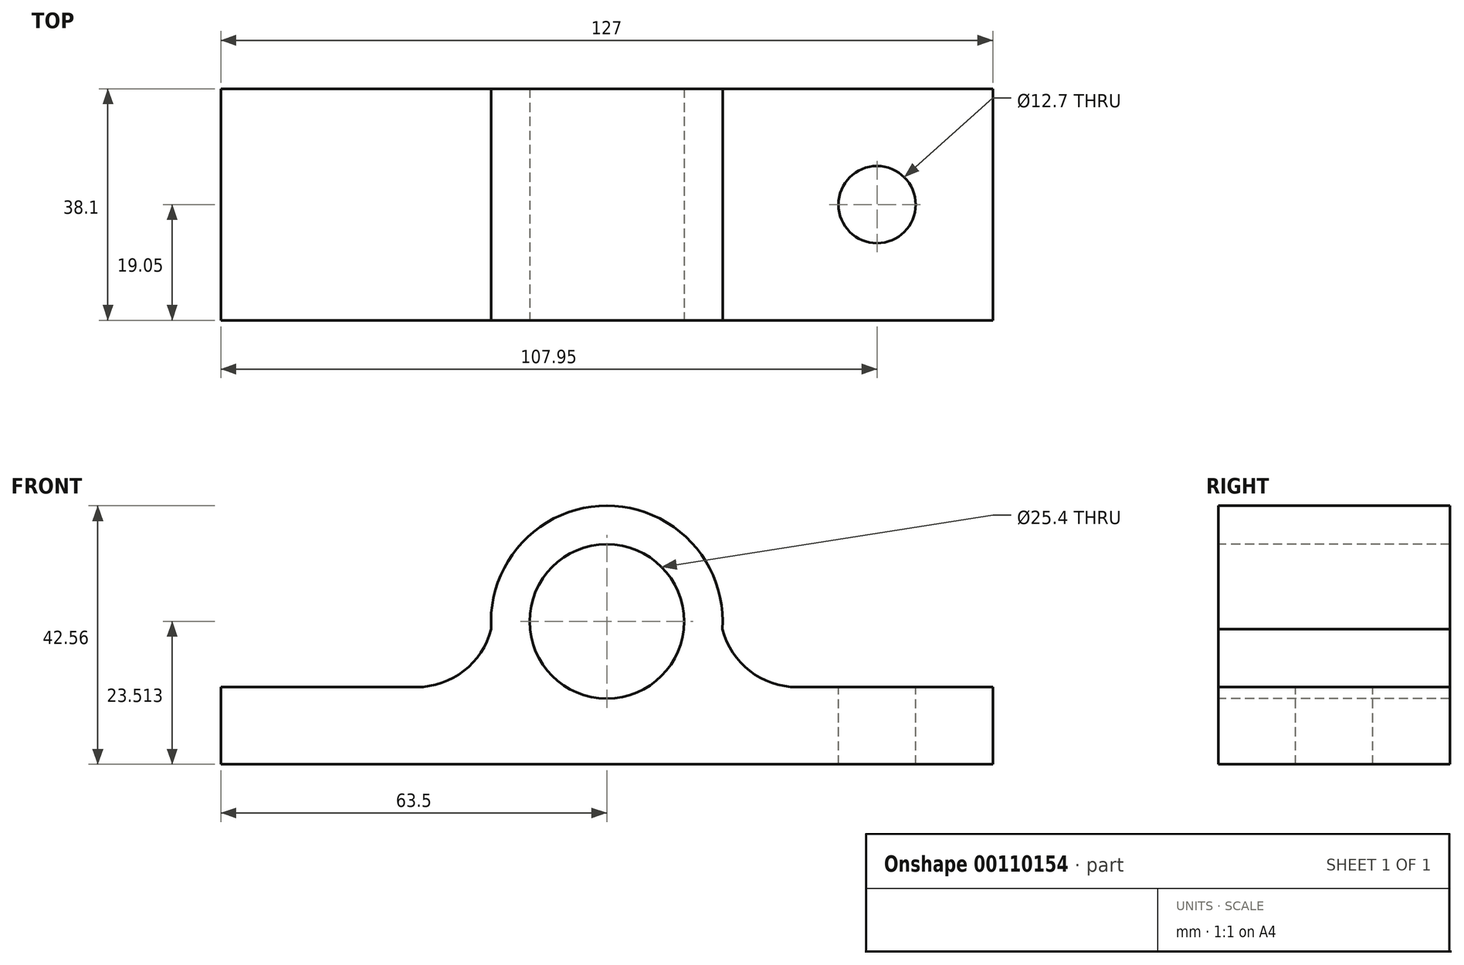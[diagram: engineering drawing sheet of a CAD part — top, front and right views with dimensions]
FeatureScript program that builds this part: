
annotation { "Feature Type Name" : "Feature", "Feature Type Description" : "" }
export const myFeature = defineFeature(function(context is Context, id is Id, definition is map)
    precondition{}
    {
        {
            var Q0;
            Q0=qCreatedBy(makeId("Front.planeOp"),FACE);
            var sketch = newSketch(context, id + "F0", { "sketchPlane" : qUnion([Q0])});
            skLineSegment(sketch, "E0", {"start": v(-63.5, 0) * mm, "end": v(63.5, 0) * mm});
            skPoint(sketch, "E1", {"position": v(0, 0) * mm});
            skLineSegment(sketch, "E2", {"start": v(-63.5, 0) * mm, "end": v(-63.5, 12.7) * mm});
            skLineSegment(sketch, "E3", {"start": v(63.5, 0) * mm, "end": v(63.5, 12.7) * mm});
            skLineSegment(sketch, "E4", {"start": v(-63.5, 12.7) * mm, "end": v(-31.32, 12.7) * mm});
            skLineSegment(sketch, "E5", {"start": v(63.5, 12.7) * mm, "end": v(31.32, 12.7) * mm});
            skPoint(sketch, "E6.visualSharp", {"position": v(-18.42, 12.7) * mm});
            skArc(sketch, "E6.filletArc", {"start": v(-31.32, 12.7) * mm, "mid": v(-23.52, 15.37) * mm, "end": v(-19, 22.26) * mm});
            skPoint(sketch, "E7.visualSharp", {"position": v(18.42, 12.7) * mm});
            skArc(sketch, "E7.filletArc", {"start": v(19, 22.26) * mm, "mid": v(23.52, 15.37) * mm, "end": v(31.32, 12.7) * mm});
            skLineSegment(sketch, "E8", {"start": v(0, 36.6) * mm, "end": v(0, 0) * mm, "construction": true});
            skArc(sketch, "E9", {"start": v(19, 22.26) * mm, "mid": v(0, 42.56) * mm, "end": v(-19, 22.26) * mm});
            skCircle(sketch, "E10", {"center": v(0, 23.51) * mm, "radius": 12.7 * mm});
            skSolve(sketch);
        }
        {
            var Q0;
            Q0=makeQuery(id+"F0.imprint","IMPRINT",FACE,{"disambiguationData":[TD([[makeQuery(id+"F0.imprint","IMPRINT",EDGE,{"derivedFrom":sQuery(id+"F0.wireOp",EDGE,"E0")}),1.0]])]});
            extrude(context, id + "F1", {"entities" : qUnion([Q0]), "oppositeDirection" : true, "depth" : 38.1 * mm});
        }
        {
            var Q0;
            Q0=makeQuery(id+"F1.opExtrude","SWEPT_FACE",FACE,{"disambiguationData":[OSD([sQuery(id+"F0.wireOp",EDGE,"E5")])]});
            var sketch = newSketch(context, id + "F2", { "sketchPlane" : qUnion([Q0])});
            skLineSegment(sketch, "E11", {"start": v(44.45, 38.1) * mm, "end": v(44.45, 0) * mm, "construction": true});
            skLineSegment(sketch, "E12", {"start": v(63.5, 19.05) * mm, "end": v(31.32, 19.05) * mm, "construction": true});
            skCircle(sketch, "E13", {"center": v(44.45, 19.05) * mm, "radius": 6.35 * mm});
            skCircle(sketch, "E14.MirrorC", {"center": v(-44.45, 19.05) * mm, "radius": 6.35 * mm});
            skLineSegment(sketch, "E15.MirrorCS", {"start": v(-44.45, 38.1) * mm, "end": v(-44.45, 0) * mm, "construction": true});
            skLineSegment(sketch, "E16.MirrorCS", {"start": v(-63.5, 19.05) * mm, "end": v(-31.32, 19.05) * mm, "construction": true});
            skSolve(sketch);
        }
        {
            var Q0;
            Q0=makeQuery(id+"F2.imprint","IMPRINT",FACE,{"disambiguationData":[TD([[makeQuery(id+"F2.imprint","IMPRINT",EDGE,{"derivedFrom":sQuery(id+"F2.wireOp",EDGE,"E14.MirrorC")}),-1.0]])]});
            var Q1;
            Q1=makeQuery(id+"F2.imprint","IMPRINT",FACE,{"disambiguationData":[TD([[makeQuery(id+"F2.imprint","IMPRINT",EDGE,{"derivedFrom":sQuery(id+"F2.wireOp",EDGE,"E13")}),1.0]])]});
            extrude(context, id + "F3", {"entities" : qUnion([Q0, Q1]), "operationType" : NewBodyOperationType.REMOVE, "oppositeDirection" : true, "depth" : 25.4 * mm});
        }
    });
